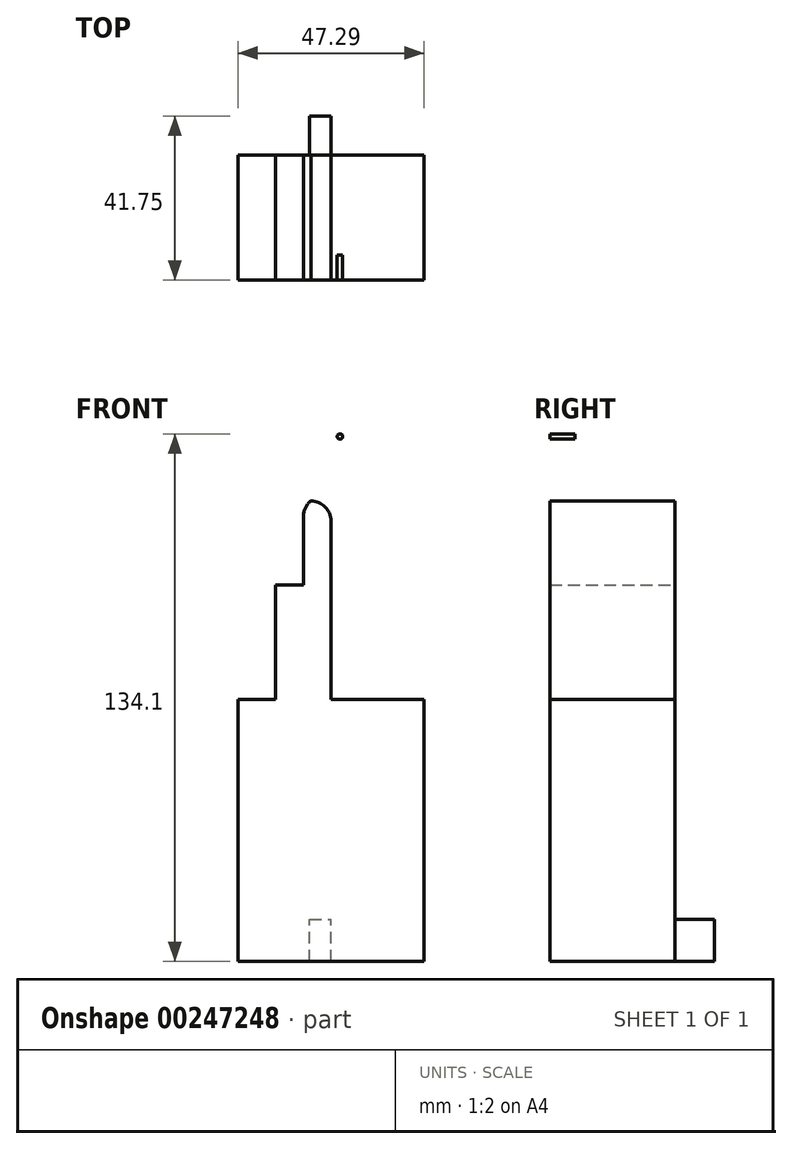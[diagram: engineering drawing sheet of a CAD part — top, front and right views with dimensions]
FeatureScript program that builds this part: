
annotation { "Feature Type Name" : "Feature", "Feature Type Description" : "" }
export const myFeature = defineFeature(function(context is Context, id is Id, definition is map)
    precondition{}
    {
        {
            var Q0;
            Q0=qCreatedBy(makeId("Front.planeOp"),FACE);
            var sketch = newSketch(context, id + "F0", { "sketchPlane" : qUnion([Q0])});
            skLineSegment(sketch, "E0.bottom", {"start": v(0, 0) * mm, "end": v(47.3, 0) * mm});
            skLineSegment(sketch, "E0.top", {"start": v(0, -66.6) * mm, "end": v(47.3, -66.6) * mm});
            skLineSegment(sketch, "E0.left", {"start": v(0, 0) * mm, "end": v(0, -66.6) * mm});
            skLineSegment(sketch, "E0.right", {"start": v(47.3, 0) * mm, "end": v(47.3, -66.6) * mm});
            skLineSegment(sketch, "E1.bottom", {"start": v(23.65, 0) * mm, "end": v(40.1, 0) * mm});
            skLineSegment(sketch, "E1.top", {"start": v(23.65, 29.05) * mm, "end": v(40.1, 29.05) * mm});
            skLineSegment(sketch, "E1.left", {"start": v(23.65, 0) * mm, "end": v(23.65, 29.05) * mm});
            skLineSegment(sketch, "E1.right", {"start": v(40.1, 0) * mm, "end": v(40.1, 29.05) * mm});
            skLineSegment(sketch, "E2.bottom", {"start": v(23.65, 29.05) * mm, "end": v(9.6, 29.05) * mm});
            skLineSegment(sketch, "E2.top", {"start": v(23.65, 0) * mm, "end": v(9.6, 0) * mm});
            skLineSegment(sketch, "E2.left", {"start": v(23.65, 29.05) * mm, "end": v(23.65, 0) * mm});
            skLineSegment(sketch, "E2.right", {"start": v(9.6, 29.05) * mm, "end": v(9.6, 0) * mm});
            skLineSegment(sketch, "E3.bottom", {"start": v(23.65, 29.05) * mm, "end": v(32.83, 29.05) * mm});
            skLineSegment(sketch, "E3.top", {"start": v(23.65, 50.43) * mm, "end": v(32.83, 50.43) * mm});
            skLineSegment(sketch, "E3.left", {"start": v(23.65, 29.05) * mm, "end": v(23.65, 50.43) * mm});
            skLineSegment(sketch, "E3.right", {"start": v(32.83, 29.05) * mm, "end": v(32.83, 50.43) * mm});
            skLineSegment(sketch, "E4.bottom", {"start": v(23.65, 50.43) * mm, "end": v(16.62, 50.43) * mm});
            skLineSegment(sketch, "E4.top", {"start": v(23.65, 29.05) * mm, "end": v(16.62, 29.05) * mm});
            skLineSegment(sketch, "E4.left", {"start": v(23.65, 50.43) * mm, "end": v(23.65, 29.05) * mm});
            skLineSegment(sketch, "E4.right", {"start": v(16.62, 50.43) * mm, "end": v(16.62, 29.05) * mm});
            skPoint(sketch, "E5.oppositeSnap0", {"position": v(28.24, 50.43) * mm});
            skLineSegment(sketch, "E5.bottom", {"start": v(23.65, 50.43) * mm, "end": v(28.24, 50.43) * mm});
            skLineSegment(sketch, "E5.top", {"start": v(23.65, 66.81) * mm, "end": v(28.24, 66.81) * mm});
            skLineSegment(sketch, "E5.left", {"start": v(23.65, 50.43) * mm, "end": v(23.65, 66.81) * mm});
            skLineSegment(sketch, "E5.right", {"start": v(28.24, 50.43) * mm, "end": v(28.24, 66.81) * mm});
            skSolve(sketch);
        }
        {
            var Q0;
            Q0=makeQuery(id+"F0.imprint","IMPRINT",FACE,{"disambiguationData":[TD([[makeQuery(id+"F0.imprint","IMPRINT",EDGE,{"derivedFrom":sQuery(id+"F0.wireOp",EDGE,"E0.top")}),1.0]])]});
            var Q1;
            Q1=makeQuery(id+"F0.imprint","IMPRINT",FACE,{"disambiguationData":[TD([[makeQuery(id+"F0.imprint","IMPRINT",EDGE,{"derivedFrom":sQuery(id+"F0.wireOp",EDGE,"E2.bottom")}),1.0]])]});
            var Q2;
            Q2=makeQuery(id+"F0.imprint","IMPRINT",FACE,{"disambiguationData":[TD([[makeQuery(id+"F0.imprint","IMPRINT",EDGE,{"derivedFrom":sQuery(id+"F0.wireOp",EDGE,"E1.bottom")}),1.0]])]});
            var Q3;
            Q3=makeQuery(id+"F0.imprint","IMPRINT",FACE,{"disambiguationData":[TD([[makeQuery(id+"F0.imprint","IMPRINT",EDGE,{"derivedFrom":sQuery(id+"F0.wireOp",EDGE,"E3.bottom")}),1.0]])]});
            var Q4;
            Q4=makeQuery(id+"F0.imprint","IMPRINT",FACE,{"disambiguationData":[TD([[makeQuery(id+"F0.imprint","IMPRINT",EDGE,{"derivedFrom":sQuery(id+"F0.wireOp",EDGE,"E4.bottom")}),1.0]])]});
            var Q5;
            Q5=makeQuery(id+"F0.imprint","IMPRINT",FACE,{"disambiguationData":[TD([[makeQuery(id+"F0.imprint","IMPRINT",EDGE,{"derivedFrom":sQuery(id+"F0.wireOp",EDGE,"E5.bottom")}),1.0]])]});
            extrude(context, id + "F1", {"entities" : qUnion([Q0, Q1, Q2, Q3, Q4, Q5]), "depth" : 25.4 * mm});
        }
        {
            var Q0;
            Q0=makeQuery(id+"F1.opExtrude","CAP_FACE",FACE,{"disambiguationData":[OSD([sQuery(id+"F0.wireOp",EDGE,"E0.bottom"),sQuery(id+"F0.wireOp",EDGE,"E0.top"),sQuery(id+"F0.wireOp",EDGE,"E0.left"),sQuery(id+"F0.wireOp",EDGE,"E0.right"),sQuery(id+"F0.wireOp",EDGE,"E1.top"),sQuery(id+"F0.wireOp",EDGE,"E1.right"),sQuery(id+"F0.wireOp",EDGE,"E2.bottom"),sQuery(id+"F0.wireOp",EDGE,"E2.right"),sQuery(id+"F0.wireOp",EDGE,"E3.top"),sQuery(id+"F0.wireOp",EDGE,"E3.right"),sQuery(id+"F0.wireOp",EDGE,"E4.bottom"),sQuery(id+"F0.wireOp",EDGE,"E4.right"),sQuery(id+"F0.wireOp",EDGE,"E5.top"),sQuery(id+"F0.wireOp",EDGE,"E5.left"),sQuery(id+"F0.wireOp",EDGE,"E5.right")])],"isStart":true});
            var sketch = newSketch(context, id + "F2", { "sketchPlane" : qUnion([Q0])});
            skLineSegment(sketch, "E6", {"start": v(-18.24, -66.6) * mm, "end": v(-18.24, -55.83) * mm});
            skLineSegment(sketch, "E7", {"start": v(-18.24, -55.83) * mm, "end": v(-23.65, -55.83) * mm});
            skPoint(sketch, "E7.endSnap0", {"position": v(-23.65, -66.6) * mm});
            skLineSegment(sketch, "E8", {"start": v(-23.65, -66.6) * mm, "end": v(-23.65, -55.83) * mm});
            skLineSegment(sketch, "E9", {"start": v(-20.94, -55.83) * mm, "end": v(-23.65, -55.83) * mm});
            skSolve(sketch);
        }
        {
            var Q0;
            {var subQ7=sQuery(id+"F2.wireOp",EDGE,"E6");Q0=makeQuery(id+"F2.imprint","IMPRINT",FACE,{"disambiguationData":[TD([[makeQuery(id+"F2.imprint","IMPRINT",EDGE,{"derivedFrom":subQ7}),-1.0]])]});}
            var sketch = newSketch(context, id + "F3", { "sketchPlane" : qUnion([Q0])});
            skSolve(sketch);
        }
        {
            var Q0;
            {var subQ1=sQuery(id+"F2.wireOp",EDGE,"E6");Q0=makeQuery(id+"F2.imprint","IMPRINT",FACE,{"disambiguationData":[TD([[makeQuery(id+"F2.imprint","IMPRINT",EDGE,{"derivedFrom":subQ1}),1.0]])]});}
            extrude(context, id + "F4", {"entities" : qUnion([Q0]), "operationType" : NewBodyOperationType.ADD, "depth" : 5 * mm});
        }
        {
            var Q0;
            Q0=makeQuery(id+"F4.opExtrude","CAP_FACE",FACE,{"disambiguationData":[OSD([sQuery(id+"F0.wireOp",EDGE,"E0.top"),sQuery(id+"F2.wireOp",EDGE,"E6"),sQuery(id+"F2.wireOp",EDGE,"E7"),sQuery(id+"F2.wireOp",EDGE,"E8"),sQuery(id+"F2.wireOp",EDGE,"E9")])],"isStart":false});
            extrude(context, id + "F5", {"entities" : qUnion([Q0]), "operationType" : NewBodyOperationType.ADD, "depth" : 5 * mm});
        }
        {
            var Q0;
            Q0=makeQuery(id+"F1.opExtrude","SWEPT_EDGE",EDGE,{"disambiguationData":[OSD([sQuery(id+"F0.wireOp",EDGE,"E3.top"),sQuery(id+"F0.wireOp",EDGE,"E3.right")])]});
            fillet(context, id + "F6", {"entities" : qUnion([Q0]), "radius" : 5.08 * mm, "tangentPropagation" : true, "allowEdgeOverflow" : false});
        }
        {
            var Q0;
            Q0=makeQuery(id+"F1.opExtrude","SWEPT_EDGE",EDGE,{"disambiguationData":[OSD([sQuery(id+"F0.wireOp",EDGE,"E4.bottom"),sQuery(id+"F0.wireOp",EDGE,"E4.right")])]});
            fillet(context, id + "F7", {"entities" : qUnion([Q0]), "radius" : 5.08 * mm, "tangentPropagation" : true, "allowEdgeOverflow" : false});
        }
        {
            var Q0;
            Q0=qCreatedBy(makeId("Front.planeOp"),FACE);
            var sketch = newSketch(context, id + "F8", { "sketchPlane" : qUnion([Q0])});
            skPoint(sketch, "E10", {"position": v(25.7, 58.17) * mm});
            skSolve(sketch);
        }
        {
            var Q0;
            Q0=sQuery(id+"F8.wireOp",VERTEX,"E10");
            var Q1;
            Q1=makeQuery(id+"F1.opExtrude","SWEPT_BODY",BODY,{"disambiguationData":[OSD([sQuery(id+"F0.wireOp",EDGE,"E0.bottom"),sQuery(id+"F0.wireOp",EDGE,"E0.top"),sQuery(id+"F0.wireOp",EDGE,"E0.left"),sQuery(id+"F0.wireOp",EDGE,"E0.right"),sQuery(id+"F0.wireOp",EDGE,"E1.top"),sQuery(id+"F0.wireOp",EDGE,"E1.right"),sQuery(id+"F0.wireOp",EDGE,"E2.bottom"),sQuery(id+"F0.wireOp",EDGE,"E2.right"),sQuery(id+"F0.wireOp",EDGE,"E3.top"),sQuery(id+"F0.wireOp",EDGE,"E3.right"),sQuery(id+"F0.wireOp",EDGE,"E4.bottom"),sQuery(id+"F0.wireOp",EDGE,"E4.right"),sQuery(id+"F0.wireOp",EDGE,"E5.top"),sQuery(id+"F0.wireOp",EDGE,"E5.left"),sQuery(id+"F0.wireOp",EDGE,"E5.right")])]});
            hole(context, id + "F9", {"style" : HoleStyle.SIMPLE, "endStyle" : HoleEndStyle.THROUGH, "oppositeDirection" : true, "holeDiameter" : 2.54 * mm, "tappedDepth" : 12.7 * mm, "tapClearance" : 3, "locations" : qUnion([Q0]), "scope" : qUnion([Q1])});
        }
        {
            var Q0;
            Q0=makeQuery(id+"F1.opExtrude","CAP_FACE",FACE,{"disambiguationData":[OSD([sQuery(id+"F0.wireOp",EDGE,"E0.bottom"),sQuery(id+"F0.wireOp",EDGE,"E0.top"),sQuery(id+"F0.wireOp",EDGE,"E0.left"),sQuery(id+"F0.wireOp",EDGE,"E0.right"),sQuery(id+"F0.wireOp",EDGE,"E1.top"),sQuery(id+"F0.wireOp",EDGE,"E1.right"),sQuery(id+"F0.wireOp",EDGE,"E2.bottom"),sQuery(id+"F0.wireOp",EDGE,"E2.right"),sQuery(id+"F0.wireOp",EDGE,"E3.top"),sQuery(id+"F0.wireOp",EDGE,"E3.right"),sQuery(id+"F0.wireOp",EDGE,"E4.bottom"),sQuery(id+"F0.wireOp",EDGE,"E4.right"),sQuery(id+"F0.wireOp",EDGE,"E5.top"),sQuery(id+"F0.wireOp",EDGE,"E5.left"),sQuery(id+"F0.wireOp",EDGE,"E5.right")])],"isStart":false});
            var sketch = newSketch(context, id + "F10", { "sketchPlane" : qUnion([Q0])});
            skCircle(sketch, "E11", {"center": v(25.94, 66.81) * mm, "radius": 0.7 * mm});
            skSolve(sketch);
        }
        {
            var Q0;
            Q0 = qSketchRegion(id + "F10", true);
            var Q1;
            {var subQ12=sQuery(id+"F0.wireOp",EDGE,"E0.top");Q1=makeQuery(id+"F10.imprint","IMPRINT",FACE,{"disambiguationData":[TD([[makeQuery(id+"F10.imprint","IMPRINT",EDGE,{"derivedFrom":makeQuery(id+"F1.opExtrude","CAP_EDGE",EDGE,{"disambiguationData":[OSD([subQ12])],"isStart":false})}),1.0]])]});}
            extrude(context, id + "F11", {"entities" : qUnion([Q0, Q1]), "operationType" : NewBodyOperationType.ADD, "depth" : 6.35 * mm});
        }
    });
